# Revit family: 4C-4_Door_High_Units_FL.rfa
name_source: partatom
category: Specialty Equipment
revit_build: Autodesk Revit 2016 (Build: 20150714_1515(x64)
units: mm (PartAtom-declared; Revit-internal decimal feet)

## family parameters
Always vertical = Yes
Cut with Voids When Loaded = No
Host = Wall
Part Type = Normal
Room Calculation Point = No
Round Connector Dimension = Use Diameter
Shared = No

## types (5) — shared parameters
Assembly Code = C1030910
Back Enclosure Material = Aluminum - Salsbury Finish = Anodized
Depth = 17.025"
Height = 16.470"
Latch Lock - Left Side = No
Latch Lock - Right Side = No
Lock Material = Stainless Steel -Salsbury Finish =  Polished
Manufacturer = Salsbury Industries
MasterFormat Number = 10 55 00
MasterFormat Title = Postal Specialties
Type Comments = 4C Standard Horizontal Mailbox - Front Loading
Version = 2.0 (08/09/16)

## per-type parameters (varying)
| type | Bottom Back Plate | Description | Door Slot L1 | Door Slot L2 | Door Slot L3 | Door Slot L4 | Door Slot R1 | Door Slot R2 | Door Slot R3 | Door Slot R4 | Latch Alignment | Left Inside Wall | Right Inside Wall | Top Back Plate | Vertical Center Divider | Width |
| 3704D-06 FL | Yes | 4 Door High Unit: 6 MB1, OM2 | 3700 Series 4C Door Configurations : MB1 Door | 3700 Series 4C Door Configurations : MB1 Door w/ Divider | 3700 Series 4C Door Configurations : MB1 Door w/ Divider | 3700 Series 4C Door Configurations : MB1 Door w/ Divider | 3700 Series 4C Door Configurations : MB1 Door | 3700 Series 4C Door Configurations : Empty | 3700 Series 4C OM2 Configuration : OM2-FL | 3700 Series 4C Door Configurations : MB1 Door w/ Divider | 14.857" | Yes | Yes | Yes | Yes | 31.098" |
| 3704S-02 FL | No | 4 Door High Unit: 2 MB1, OM2 | 3700 Series 4C Door Configurations : Empty | 3700 Series 4C Door Configurations : Empty | 3700 Series 4C Door Configurations : Empty | 3700 Series 4C Door Configurations : Empty | 3700 Series 4C Door Configurations : MB1 Door | 3700 Series 4C Door Configurations : Empty | 3700 Series 4C OM2 Configuration : OM2-FL | 3700 Series 4C Door Configurations : MB1 Door w/ Divider | 13.876" | No | No | No | No | 16.344" |
| 3704S-01 FL | No | 4 Door High Unit: 1 MB2, OM2 | 3700 Series 4C Door Configurations : Empty | 3700 Series 4C Door Configurations : Empty | 3700 Series 4C Door Configurations : Empty | 3700 Series 4C Door Configurations : Empty | 3700 Series 4C Door Configurations : Empty | 3700 Series 4C OM2 Configuration : OM2-FL | 3700 Series 4C Door Configurations : Empty | 3700 Series 4C Door Configurations : MB2 Door w/ Divider | 13.876" | No | No | No | No | 16.344" |
| 3704S-1P FL | No | 4 Door High Unit: 1 PL4 | 3700 Series 4C Door Configurations : Empty | 3700 Series 4C Door Configurations : Empty | 3700 Series 4C Door Configurations : Empty | 3700 Series 4C Door Configurations : Empty | 3700 Series 4C Door Configurations : Empty | 3700 Series 4C Door Configurations : Empty | 3700 Series 4C Door Configurations : Empty | 3700 Series 4C Parcel Configurations : PL4 | 13.876" | No | No | No | No | 16.344" |
| 3704D-2P FL | Yes | 4 Door High Unit: 2 PL4 | 3700 Series 4C Door Configurations : Empty | 3700 Series 4C Door Configurations : Empty | 3700 Series 4C Door Configurations : Empty | 3700 Series 4C Parcel Configurations : PL4 | 3700 Series 4C Door Configurations : Empty | 3700 Series 4C Door Configurations : Empty | 3700 Series 4C Door Configurations : Empty | 3700 Series 4C Parcel Configurations : PL4 | 14.857" | Yes | Yes | Yes | Yes | 31.098" |

note: column(s) folded — value = type name in every type: Model

## geometry (parser evidence)
native form markers: Blend x18, Extrusion x13, Sweep x72
no freeform markers — native parametric forms only
